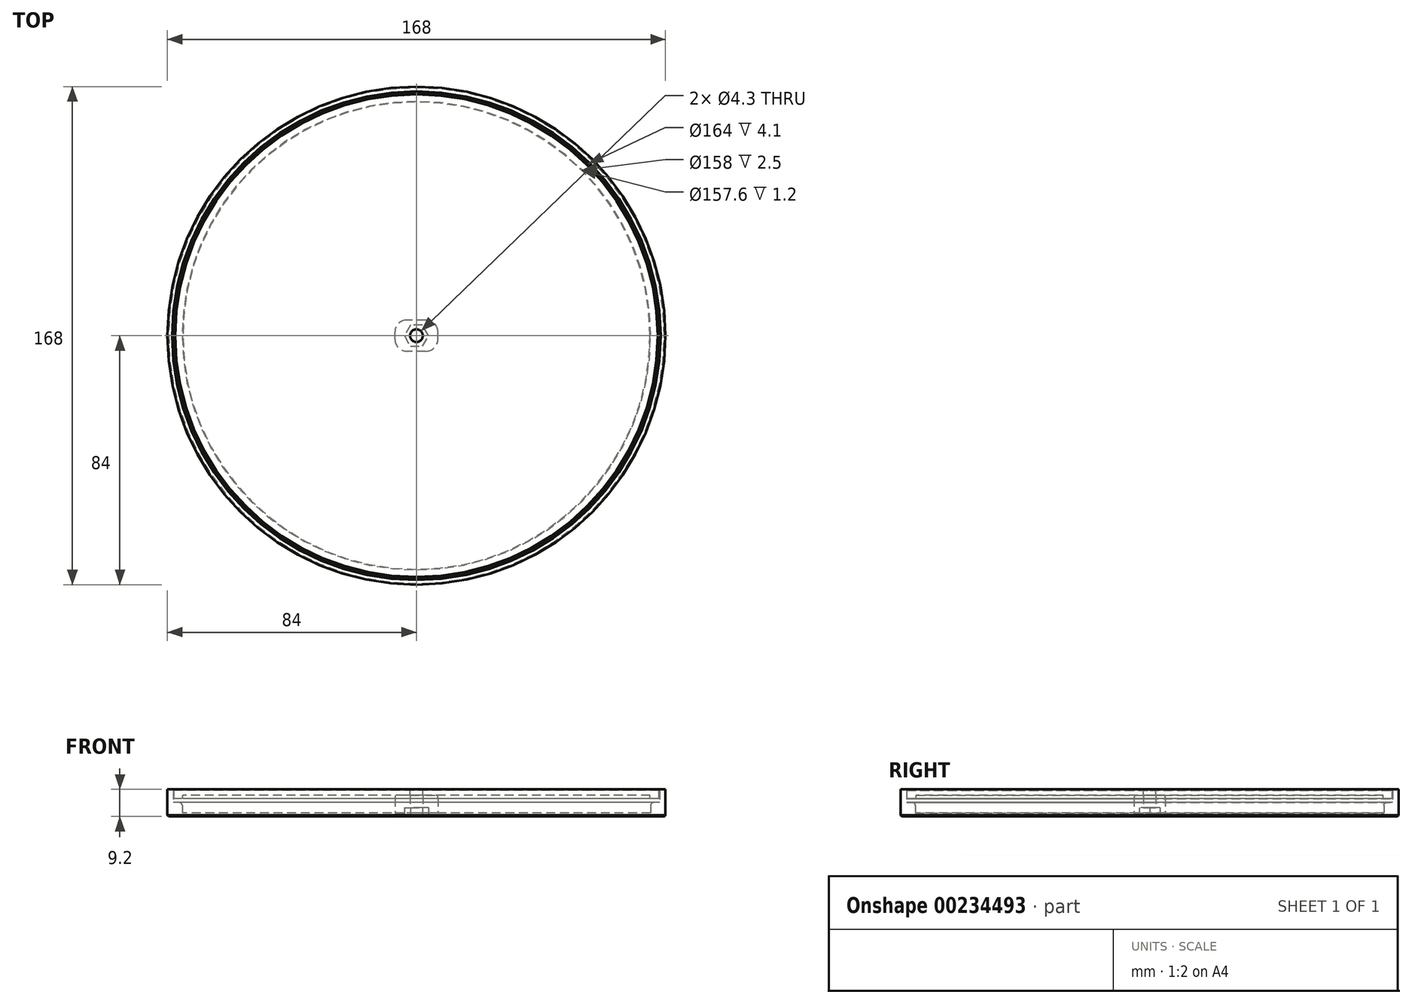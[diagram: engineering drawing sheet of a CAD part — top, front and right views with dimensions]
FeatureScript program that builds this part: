
annotation { "Feature Type Name" : "Feature", "Feature Type Description" : "" }
export const myFeature = defineFeature(function(context is Context, id is Id, definition is map)
    precondition{}
    {
        {
            var Q0;
            Q0=qCreatedBy(makeId("Top.planeOp"),FACE);
            var sketch = newSketch(context, id + "F0", { "sketchPlane" : qUnion([Q0])});
            skCircle(sketch, "E0", {"center": v(0, 0) * mm, "radius": 84 * mm});
            skSolve(sketch);
        }
        {
            var Q0;
            Q0 = qSketchRegion(id + "F0", true);
            extrude(context, id + "F1", {"entities" : qUnion([Q0]), "depth" : 1.2 * mm, "offsetDistance" : 25 * mm});
        }
        {
            var Q0;
            Q0=makeQuery(id+"F1.opExtrude","CAP_FACE",FACE,{"disambiguationData":[OSD([sQuery(id+"F0.wireOp",EDGE,"E0")])],"isStart":false});
            var sketch = newSketch(context, id + "F2", { "sketchPlane" : qUnion([Q0])});
            skCircle(sketch, "E1.0", {"center": v(0, 0) * mm, "radius": 84 * mm});
            skCircle(sketch, "E2.0", {"center": v(0, 0) * mm, "radius": 82 * mm});
            skSolve(sketch);
        }
        {
            var Q0;
            Q0 = qSketchRegion(id + "F2", true);
            extrude(context, id + "F3", {"entities" : qUnion([Q0]), "operationType" : NewBodyOperationType.ADD, "depth" : 8 * mm, "offsetDistance" : 25 * mm});
        }
        {
            var Q0;
            Q0=makeQuery(id+"F1.opExtrude","CAP_FACE",FACE,{"disambiguationData":[OSD([sQuery(id+"F0.wireOp",EDGE,"E0")])],"isStart":false});
            var sketch = newSketch(context, id + "F4", { "sketchPlane" : qUnion([Q0])});
            skCircle(sketch, "E3.0", {"center": v(0, 0) * mm, "radius": 82 * mm});
            skCircle(sketch, "E4.0", {"center": v(0, 0) * mm, "radius": 79 * mm});
            skSolve(sketch);
        }
        {
            var Q0;
            Q0 = qSketchRegion(id + "F4", true);
            extrude(context, id + "F5", {"entities" : qUnion([Q0]), "operationType" : NewBodyOperationType.ADD, "depth" : 3.5 * mm, "offsetDistance" : 25 * mm});
        }
        {
            var Q0;
            Q0=makeQuery(id+"F5.opExtrude","CAP_EDGE",EDGE,{"disambiguationData":[OSD([sQuery(id+"F4.wireOp",EDGE,"E4.0")])],"isStart":false});
            fillet(context, id + "F6", {"entities" : qUnion([Q0]), "tangentPropagation" : true, "radius" : 1 * mm, "defaultsChanged" : false, "vertexSettings" : [], "allowEdgeOverflow" : false});
        }
        {
            var Q0;
            Q0=makeQuery(id+"F1.opExtrude","CAP_FACE",FACE,{"disambiguationData":[OSD([sQuery(id+"F0.wireOp",EDGE,"E0")])],"isStart":false});
            var sketch = newSketch(context, id + "F7", { "sketchPlane" : qUnion([Q0])});
            skLineSegment(sketch, "E5.bottom", {"start": v(3.25, -5.25) * mm, "end": v(-3.25, -5.25) * mm});
            skLineSegment(sketch, "E5.top", {"start": v(3.25, 5.25) * mm, "end": v(-3.25, 5.25) * mm});
            skLineSegment(sketch, "E5.left", {"start": v(7.25, -1.25) * mm, "end": v(7.25, 1.25) * mm});
            skLineSegment(sketch, "E5.right", {"start": v(-7.25, -1.25) * mm, "end": v(-7.25, 1.25) * mm});
            skPoint(sketch, "E5.middle", {"position": v(0, 0) * mm});
            skPoint(sketch, "E6.visualSharp", {"position": v(-7.25, 5.25) * mm});
            skArc(sketch, "E6.filletArc", {"start": v(-3.25, 5.25) * mm, "mid": v(-6.08, 4.08) * mm, "end": v(-7.25, 1.25) * mm});
            skPoint(sketch, "E7.visualSharp", {"position": v(7.25, 5.25) * mm});
            skArc(sketch, "E7.filletArc", {"start": v(7.25, 1.25) * mm, "mid": v(6.08, 4.08) * mm, "end": v(3.25, 5.25) * mm});
            skPoint(sketch, "E8.visualSharp", {"position": v(7.25, -5.25) * mm});
            skArc(sketch, "E8.filletArc", {"start": v(3.25, -5.25) * mm, "mid": v(6.08, -4.08) * mm, "end": v(7.25, -1.25) * mm});
            skPoint(sketch, "E9.visualSharp", {"position": v(-7.25, -5.25) * mm});
            skArc(sketch, "E9.filletArc", {"start": v(-7.25, -1.25) * mm, "mid": v(-6.08, -4.08) * mm, "end": v(-3.25, -5.25) * mm});
            skSolve(sketch);
        }
        {
            var Q0;
            Q0 = qSketchRegion(id + "F7", true);
            extrude(context, id + "F8", {"entities" : qUnion([Q0]), "operationType" : NewBodyOperationType.ADD, "depth" : 6 * mm, "offsetDistance" : 25 * mm});
        }
        {
            var Q0;
            Q0=makeQuery(id+"F1.opExtrude","CAP_FACE",FACE,{"disambiguationData":[OSD([sQuery(id+"F0.wireOp",EDGE,"E0")])],"isStart":true});
            var sketch = newSketch(context, id + "F9", { "sketchPlane" : qUnion([Q0])});
            skCircle(sketch, "E10", {"center": v(0, 0) * mm, "radius": 2.15 * mm});
            skSolve(sketch);
        }
        {
            var Q0;
            Q0 = qSketchRegion(id + "F9", true);
            extrude(context, id + "F10", {"entities" : qUnion([Q0]), "operationType" : NewBodyOperationType.REMOVE, "endBound" : BoundingType.THROUGH_ALL, "oppositeDirection" : true, "depth" : 25 * mm, "offsetDistance" : 25 * mm});
        }
        {
            var Q0;
            Q0=makeQuery(id+"F1.opExtrude","CAP_FACE",FACE,{"disambiguationData":[OSD([sQuery(id+"F0.wireOp",EDGE,"E0")])],"isStart":true});
            var sketch = newSketch(context, id + "F11", { "sketchPlane" : qUnion([Q0])});
            skCircle(sketch, "E11.cCircle", {"center": v(0, 0) * mm, "radius": 3.55 * mm, "construction": true});
            skLineSegment(sketch, "E11.0", {"start": v(-4.1, 0) * mm, "end": v(-2.05, 3.55) * mm});
            skLineSegment(sketch, "E11.1", {"start": v(-2.05, 3.55) * mm, "end": v(2.05, 3.55) * mm});
            skLineSegment(sketch, "E11.2", {"start": v(2.05, 3.55) * mm, "end": v(4.1, 0) * mm});
            skLineSegment(sketch, "E11.3", {"start": v(4.1, 0) * mm, "end": v(2.05, -3.55) * mm});
            skLineSegment(sketch, "E11.4", {"start": v(2.05, -3.55) * mm, "end": v(-2.05, -3.55) * mm});
            skLineSegment(sketch, "E11.5", {"start": v(-2.05, -3.55) * mm, "end": v(-4.1, 0) * mm});
            skPoint(sketch, "E11.0.midPoint", {"position": v(-3.07, 1.78) * mm});
            skSolve(sketch);
        }
        {
            var Q0;
            Q0 = qSketchRegion(id + "F11", true);
            extrude(context, id + "F12", {"entities" : qUnion([Q0]), "operationType" : NewBodyOperationType.REMOVE, "oppositeDirection" : true, "depth" : 3 * mm, "offsetDistance" : 25 * mm});
        }
        {
            var Q0;
            Q0=makeQuery(id+"F8.opExtrude","CAP_EDGE",EDGE,{"disambiguationData":[OSD([sQuery(id+"F7.wireOp",EDGE,"E7.filletArc")])],"isStart":false});
            fillet(context, id + "F13", {"entities" : qUnion([Q0]), "tangentPropagation" : true, "radius" : 0.8 * mm, "defaultsChanged" : true, "vertexSettings" : [], "allowEdgeOverflow" : false});
        }
        {
            var Q0;
            Q0=makeQuery(id+"F3.opExtrude","CAP_EDGE",EDGE,{"disambiguationData":[OSD([sQuery(id+"F2.wireOp",EDGE,"E2.0")])],"isStart":false});
            var Q1;
            Q1=makeQuery(id+"F1.opExtrude","CAP_EDGE",EDGE,{"disambiguationData":[OSD([sQuery(id+"F0.wireOp",EDGE,"E0")])],"isStart":true});
            chamfer(context, id + "F14", {"entities" : qUnion([Q0, Q1]), "width" : 0.4 * mm, "tangentPropagation" : true});
        }
        {
            var Q0;
            Q0=makeQuery(id+"F3.opExtrude","CAP_FACE",FACE,{"disambiguationData":[OSD([sQuery(id+"F2.wireOp",EDGE,"E1.0"),sQuery(id+"F2.wireOp",EDGE,"E2.0")])],"isStart":false});
            var sketch = newSketch(context, id + "F15", { "sketchPlane" : qUnion([Q0])});
            skCircle(sketch, "E12.0", {"center": v(0, 0) * mm, "radius": 81.8 * mm});
            skCircle(sketch, "E13.0", {"center": v(0, 0) * mm, "radius": 2.15 * mm});
            skSolve(sketch);
        }
        {
            var Q0;
            Q0 = qSketchRegion(id + "F15", true);
            var Q1;
            Q1=makeQuery(id+"F8.opExtrude","CAP_FACE",FACE,{"disambiguationData":[OSD([sQuery(id+"F7.wireOp",EDGE,"E5.bottom"),sQuery(id+"F7.wireOp",EDGE,"E5.top"),sQuery(id+"F7.wireOp",EDGE,"E5.left"),sQuery(id+"F7.wireOp",EDGE,"E5.right"),sQuery(id+"F7.wireOp",EDGE,"E6.filletArc"),sQuery(id+"F7.wireOp",EDGE,"E7.filletArc"),sQuery(id+"F7.wireOp",EDGE,"E8.filletArc"),sQuery(id+"F7.wireOp",EDGE,"E9.filletArc")])],"isStart":false});
            extrude(context, id + "F16", {"entities" : qUnion([Q0]), "endBound" : BoundingType.UP_TO_SURFACE, "oppositeDirection" : true, "depth" : 25 * mm, "endBoundEntityFace" : qUnion([Q1]), "offsetDistance" : 25 * mm});
        }
        {
            var Q0;
            Q0=makeQuery(id+"F16.opExtrude","CAP_FACE",FACE,{"disambiguationData":[OSD([sQuery(id+"F15.wireOp",EDGE,"E12.0"),sQuery(id+"F15.wireOp",EDGE,"E13.0")])],"isStart":true});
            var sketch = newSketch(context, id + "F17", { "sketchPlane" : qUnion([Q0])});
            skCircle(sketch, "E14.0", {"center": v(0, 0) * mm, "radius": 81.8 * mm});
            skCircle(sketch, "E15.0", {"center": v(0, 0) * mm, "radius": 78.8 * mm});
            skSolve(sketch);
        }
        {
            var Q0;
            Q0 = qSketchRegion(id + "F17", true);
            extrude(context, id + "F18", {"entities" : qUnion([Q0]), "operationType" : NewBodyOperationType.ADD, "oppositeDirection" : true, "depth" : 3.2 * mm, "offsetDistance" : 25 * mm});
        }
        {
            var Q0;
            Q0=makeQuery(id+"F16.opExtrude","CAP_EDGE",EDGE,{"disambiguationData":[OSD([sQuery(id+"F15.wireOp",EDGE,"E12.0")])],"isStart":true});
            chamfer(context, id + "F19", {"entities" : qUnion([Q0]), "width" : 0.4 * mm, "tangentPropagation" : true});
        }
    });
